# Revit family: KS Husky, Typ II-13, Ø160-168,3
name_source: partatom
category: HLS-Bauteile
revit_build: Autodesk Revit 2018 (Build: 20190510_1515(x64)
units: mm (PartAtom-declared; Revit-internal decimal feet)

## family parameters
Arbeitsebenenbasiert = Ja
Beim Laden mit Abzugskörper schneiden = Nein
Bemaßung runder Anschluss = Durchmesser verwenden
Gemeinsam genutzt = Ja
Immer vertikal = Nein
Raumberechnungspunkt = Nein
Teiletyp = Normal

## types (2) — shared parameters
Anschluss = M10/M12
Baustoffklasse = B2
DVS = 18 mm  [stored 0.0590551 ft]
Dichte Kern = 120 kg/m³
Dämmkörper = KA/PU
Fabrikat = MEFA
Firma = MEFA Befestigungs- und Montagesysteme GmbH
HGA = 22 mm  [stored 0.0721785 ft]
Kurztext1 = Kälteschelle Husky II 13
L = 51 mm  [stored 0.167323 ft]
MB = 35 mm  [stored 0.114829 ft]
MD = 4 mm  [stored 0.0131234 ft]
Material = Stahl
Material Mantel = Kunststoff
Materialname = S235
Mengeneinheit = St
Oberflaeche = galvanisch verzinkt
Rohrschellentyp = Maxima PSM
Schalenlänge = 51 mm
Typ = II 13
Vorgabe-Ansicht = 1219 mm
Wasserdampfdiffusionswiderstand = 7000 µ
Wärmeleitfähigkeit = 0.029 W/mK
max. Temperaturbeständigkeit = 105 °C
mittl. Nenndruckfestigkeit Kern = 1,35 N/mm²
stat. Belastung Kern = 0,27 N/mm²

## per-type parameters (varying)
- Kälteschelle Husky, Typ II-13, M10/M12, Ø160: A=43 mm; AB=2 mm  [stored 0.00656168 ft]; Anschlußhöhe=42 mm; Artikelnummer=6831600; B=265 mm  [stored 0.869423 ft]; Breite=265 mm  [stored 0.869423 ft]; D=160 mm  [stored 0.524934 ft]; D0=193 mm  [stored 0.633202 ft]; DF1=32 mm  [stored 0.104987 ft]; DF2=32 mm  [stored 0.104987 ft]; DS=17 mm; Dmax=160 mm  [stored 0.524934 ft]; Dmin=158 mm; Dämmstärke=17 mm; EAN=4250928440648; Gewicht=0.99 kg; Gewicht pro Bauteil=0.99 kg; H=223 mm; Kurztext2=160 mm Iso 17 x 51 mm M10/M12; R=97 mm; RM=101 mm; Rohraußendurchmesser Kunststoff=160 mm; S=233 mm; max. zul. Last=1.91 kN; vpe=4 St
- Kälteschelle Husky, Typ II-13, M10/M12, Ø168,3: A=42 mm; AB=3 mm  [stored 0.00984252 ft]; Anschlußhöhe=41 mm; Artikelnummer=6831680; B=272 mm; Breite=272 mm; D=168 mm; D0=200 mm  [stored 0.656168 ft]; DF1=31 mm  [stored 0.101706 ft]; DF2=31 mm  [stored 0.101706 ft]; DS=16 mm  [stored 0.0524934 ft]; Dmax=170 mm  [stored 0.557743 ft]; Dmin=165 mm; Dämmstärke=16 mm  [stored 0.0524934 ft]; EAN=4250928440655; Gewicht=1.02 kg; Gewicht pro Bauteil=1.02 kg; H=230 mm; Kurztext2=168,3 mm Iso 16 x 51 mm M10/M12; R=100 mm  [stored 0.328084 ft]; RM=104 mm; Rohraußendurchmesser Stahl=168,3 mm; S=241 mm; max. zul. Last=1.98 kN; vpe=2 St

note: [stored X ft] marks values corroborated as IEEE doubles in the binary element streams (Revit-internal decimal feet)

## geometry (parser evidence)
native form markers: Sweep x2
no freeform markers — native parametric forms only
